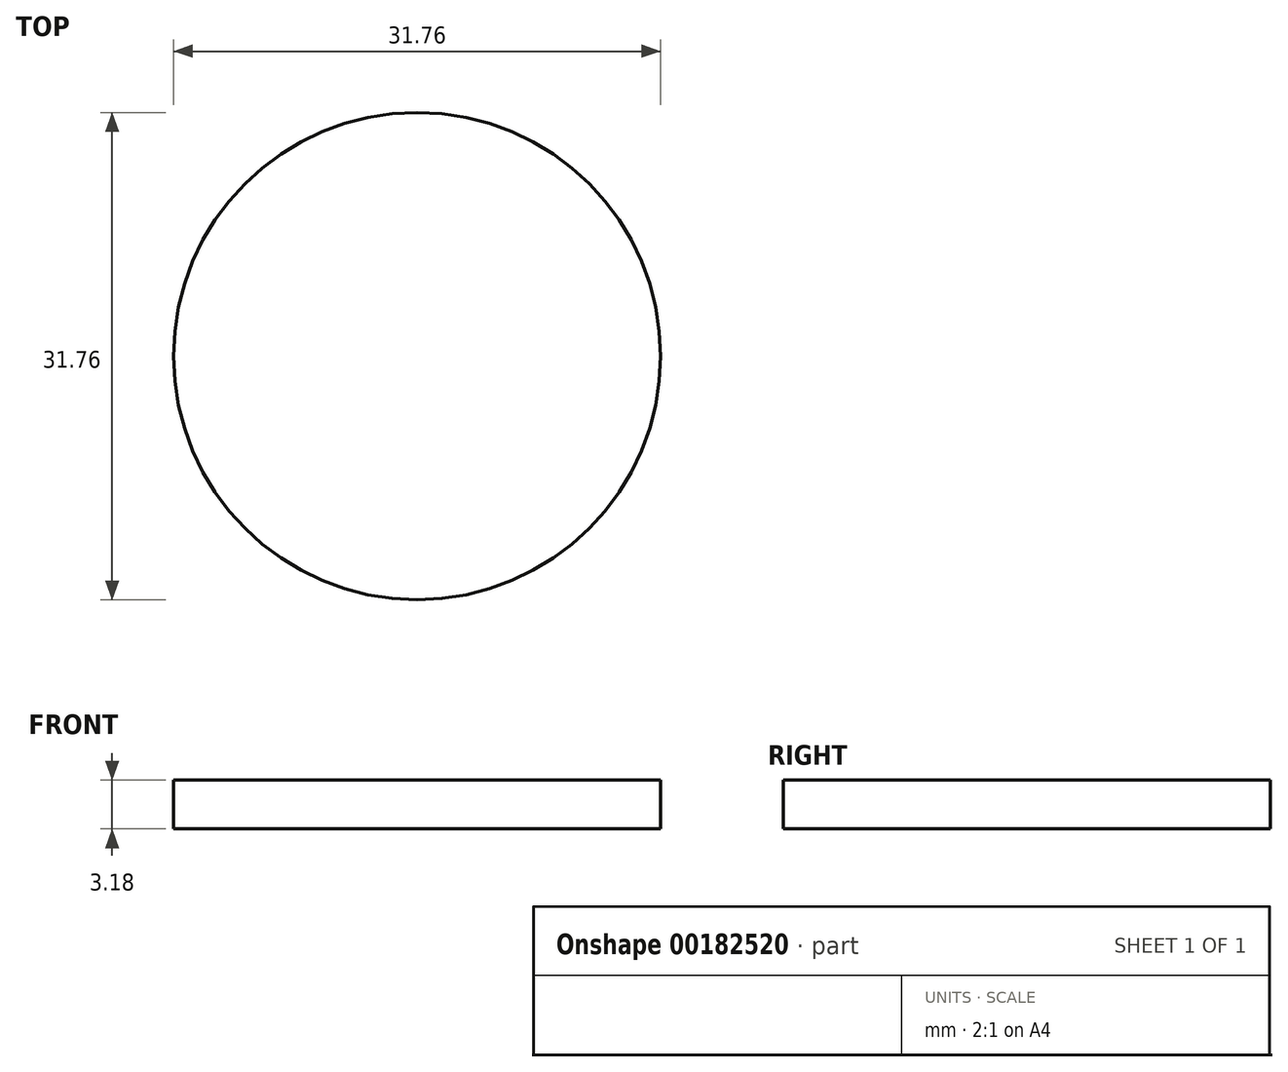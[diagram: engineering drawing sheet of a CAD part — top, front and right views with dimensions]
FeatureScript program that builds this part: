
annotation { "Feature Type Name" : "Feature", "Feature Type Description" : "" }
export const myFeature = defineFeature(function(context is Context, id is Id, definition is map)
    precondition{}
    {
        {
            var Q0;
            Q0=qCreatedBy(makeId("Top.planeOp"),FACE);
            var sketch = newSketch(context, id + "F0", { "sketchPlane" : qUnion([Q0])});
            skCircle(sketch, "E0", {"center": v(0, 0) * mm, "radius": 15.88 * mm});
            skSolve(sketch);
        }
        {
            var Q0;
            Q0=makeQuery(id+"F0.imprint","IMPRINT",FACE,{"disambiguationData":[TD([[makeQuery(id+"F0.imprint","IMPRINT",EDGE,{"derivedFrom":sQuery(id+"F0.wireOp",EDGE,"E0")}),1.0]])]});
            extrude(context, id + "F1", {"entities" : qUnion([Q0]), "depth" : 3.17 * mm});
        }
    });
